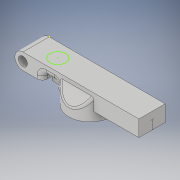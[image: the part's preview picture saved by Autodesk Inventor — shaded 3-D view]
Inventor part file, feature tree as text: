
AUTODESK INVENTOR PART (.ipt)
format: ipt  version: 2019 (Build 230136000, 136)  size: 350,208 bytes
history: native  units: in
note: dims shown in document units (in); Inventor stores cm internally (conversion verified against a paired STEP export)
features: sketch x8, extrude x7, fillet x6, chamfer x2
ambient origin geometry x8: Origin, YZ Plane, XZ Plane, XY Plane, X Axis, Y Axis, Z Axis, Center Point
bodies: Solid1 (feature_tree)
feature tree (23):
  extrude  "Extrusion1"  Depth=2.5709in
  extrude  "Extrusion2"  Depth=0.5827in TaperAngle=0.0deg
  extrude  "Extrusion3"  Depth=0.1969in TaperAngle=0.0deg
  chamfer  "Chamfer3"  Distance=0.1969in
  chamfer  "Chamfer4"  Distance=0.5827in
  fillet  "Fillet4"  Radius=0.2756in
  fillet  "Fillet5"  Radius=0.1811in
  extrude  "Extrusion6"  Depth=0.0787in
  extrude  "Extrusion7"  Depth=0.0787in
  extrude  "Extrusion8"  Depth=0.8661in
  extrude  "Extrusion9"  Depth=0.0394in TaperAngle=0.0deg
  fillet  "Fillet6"  Radius=0.5827in
  fillet  "Fillet7"  Radius=0.2913in
  fillet  "Fillet8"  Radius=0.0787in
  fillet  "Fillet9"  Radius=0.0394in
  sketch  "Sketch14"  dims[d30=1.378in d45=0.5827in d46=0.2756in d47=0.1811in d48=120.0deg d49=0.1811in d50=0.2756in d51=120.0deg d52=0.0787in d53=0.0787in d54=0.8661in d55=0.0394in d56=0.0in d57=0.5827in d58=0.2913in d63=0.0787in d64=0.0394in d65=0.5827in d66=0.0in d67=0.1575in d68=0.5827in d69=0.2126in d70=0.2362in d71=0.0in d72=0.0787in d73=0.1575in d74=0.0787in d75=0.0787in d76=0.1575in d77=0.0in d78=0.1181in d79=0.0394in d80=0.0394in d81=0.0394in]
  sketch  "Sketch1"  dims[d0=0.2008in d2=2.5709in]
  sketch  "Sketch2"  dims[d3=0.1791in d4=0.5827in d5=0.0in]
  sketch  "Sketch3"  dims[d6=0.5118in d7=0.1969in d8=0.0in]
  sketch  "Sketch10"  dims[d9=2.315in]
  sketch  "Sketch11"  dims[d11=0.9449in d13=0.1969in d14=0.0in]
  sketch  "Sketch12"  dims[d15=0.2913in]
  sketch  "Sketch13"  dims[d16=0.2913in]
